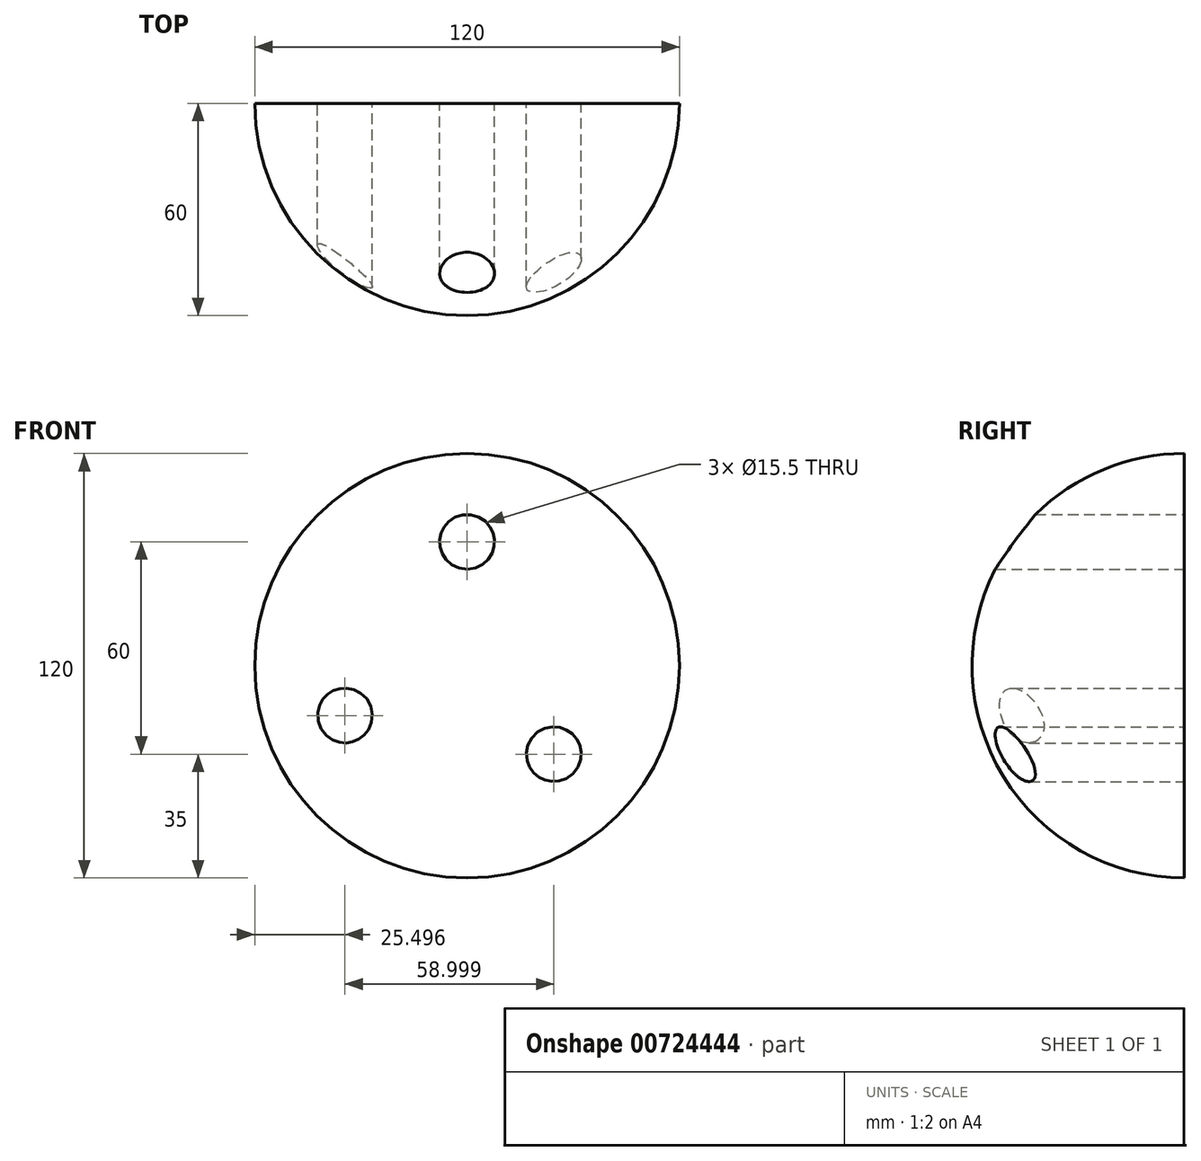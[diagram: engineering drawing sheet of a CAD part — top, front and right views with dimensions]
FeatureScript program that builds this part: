
annotation { "Feature Type Name" : "Feature", "Feature Type Description" : "" }
export const myFeature = defineFeature(function(context is Context, id is Id, definition is map)
    precondition{}
    {
        {
            var Q0;
            Q0=qCreatedBy(makeId("Front.planeOp"),FACE);
            var sketch = newSketch(context, id + "F0", { "sketchPlane" : qUnion([Q0])});
            skArc(sketch, "E0", {"start": v(0, -60) * mm, "mid": v(60, 0) * mm, "end": v(0, 60) * mm});
            skLineSegment(sketch, "E1", {"start": v(0, 60) * mm, "end": v(0, -60) * mm});
            skSolve(sketch);
        }
        {
            var Q0;
            Q0=makeQuery(id+"F0.imprint","IMPRINT",FACE,{"disambiguationData":[TD([[makeQuery(id+"F0.imprint","IMPRINT",EDGE,{"derivedFrom":sQuery(id+"F0.wireOp",EDGE,"E0")}),1.0]])]});
            var Q1;
            Q1=sQuery(id+"F0.wireOp",EDGE,"E1");
            revolve(context, id + "F1", {"surfaceOperationType" : NewSurfaceOperationType.NEW, "entities" : qUnion([Q0]), "axis" : qUnion([Q1]), "revolveType" : RevolveType.ONE_DIRECTION, "angle" : 180 * degree});
        }
        {
            var Q0;
            Q0=qCreatedBy(makeId("Front.planeOp"),FACE);
            var sketch = newSketch(context, id + "F2", { "sketchPlane" : qUnion([Q0])});
            skCircle(sketch, "E2", {"center": v(0, 35) * mm, "radius": 7.75 * mm});
            skCircle(sketch, "E3", {"center": v(-34.5, -14.09) * mm, "radius": 7.75 * mm});
            skCircle(sketch, "E4", {"center": v(24.5, -25) * mm, "radius": 7.75 * mm});
            skSolve(sketch);
        }
        {
            var Q0;
            Q0=makeQuery(id+"F2.imprint","IMPRINT",FACE,{"disambiguationData":[TD([[makeQuery(id+"F2.imprint","IMPRINT",EDGE,{"derivedFrom":sQuery(id+"F2.wireOp",EDGE,"E2")}),1.0]])]});
            var Q1;
            Q1=makeQuery(id+"F2.imprint","IMPRINT",FACE,{"disambiguationData":[TD([[makeQuery(id+"F2.imprint","IMPRINT",EDGE,{"derivedFrom":sQuery(id+"F2.wireOp",EDGE,"E3")}),1.0]])]});
            var Q2;
            Q2=makeQuery(id+"F2.imprint","IMPRINT",FACE,{"disambiguationData":[TD([[makeQuery(id+"F2.imprint","IMPRINT",EDGE,{"derivedFrom":sQuery(id+"F2.wireOp",EDGE,"E4")}),1.0]])]});
            extrude(context, id + "F3", {"entities" : qUnion([Q0, Q1, Q2]), "operationType" : NewBodyOperationType.REMOVE, "depth" : 116 * mm, "offsetDistance" : 25 * mm});
        }
    });
